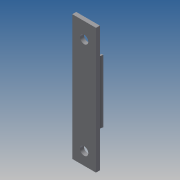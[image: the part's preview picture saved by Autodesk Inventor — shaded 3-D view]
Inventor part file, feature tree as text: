
AUTODESK INVENTOR PART (.ipt)
format: ipt  version: 2014 SP1 (Build 180222100, 222)  size: 92,672 bytes
history: native  units: in
note: dims shown in document units (in); Inventor stores cm internally (conversion verified against a paired STEP export)
features: sketch x4, extrude x2, plane x1, hole x1
ambient origin geometry x8: Origin, YZ Plane, XZ Plane, XY Plane, X Axis, Y Axis, Z Axis, Center Point
bodies: Solid1 (feature_tree)
feature tree (8):
  extrude  "Extrusion1"  Depth=0.05in
  sketch  "Sketch2"  dims[d2=2.0in d3=0.0in d4=4.0in]
  plane  "Work Plane1"
  extrude  "Extrusion2"  Depth=4.0in
  hole  "Hole1"  [1 undecoded]
  sketch  "Sketch1"  dims[d0=0.5in d1=0.05in]
  sketch  "Sketch3"  dims[d5=0.125in d6=0.0in]
  sketch  "Sketch4"  dims[d7=0.266in d8=0.75in d9=0.507in d10=0.25in d11=0.5635in d12=1.0in d13=0.8108in]
note: 1 required parameter value undecoded (feature->parameter linkage not recoverable at this tier; creation-order binding heuristic only, values carry confidence <= 0.55)
